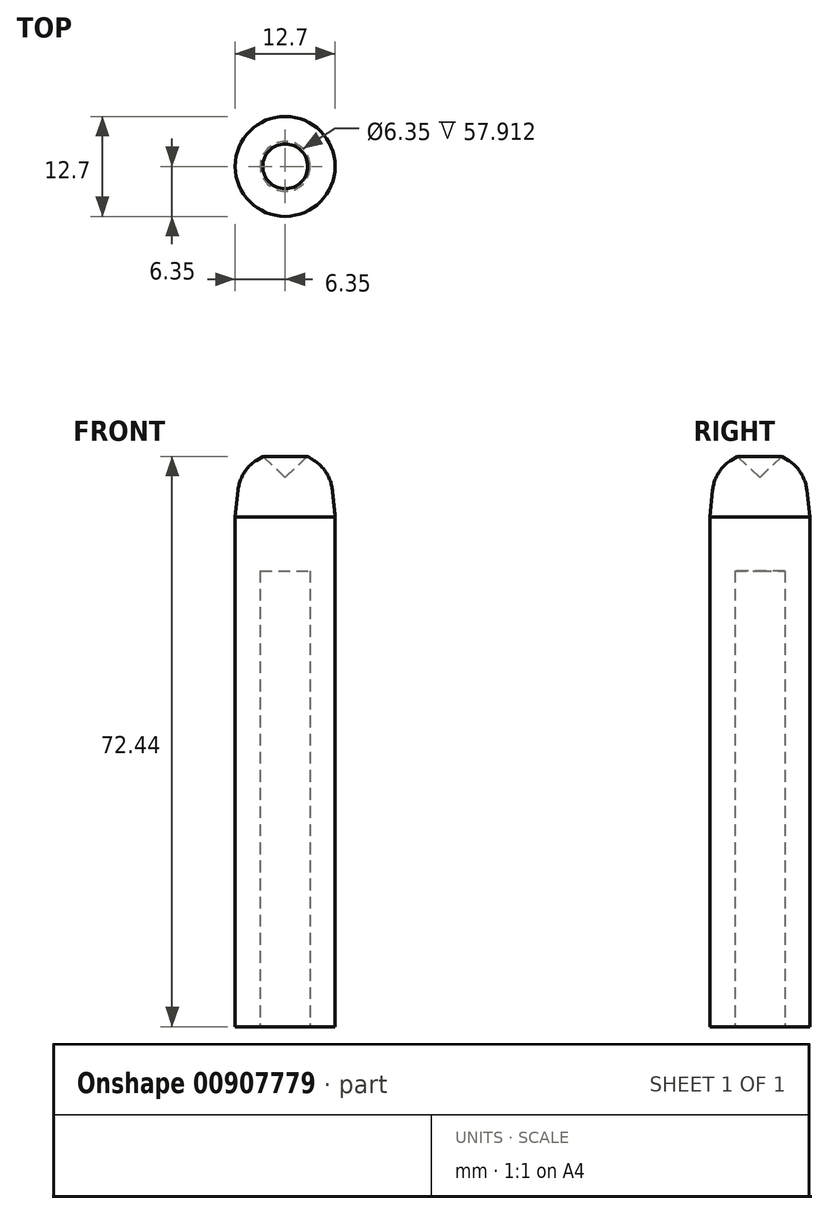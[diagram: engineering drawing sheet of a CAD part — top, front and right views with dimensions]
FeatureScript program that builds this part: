
annotation { "Feature Type Name" : "Feature", "Feature Type Description" : "" }
export const myFeature = defineFeature(function(context is Context, id is Id, definition is map)
    precondition{}
    {
        {
            var Q0;
            Q0=qCreatedBy(makeId("Top.planeOp"),FACE);
            var sketch = newSketch(context, id + "F0", { "sketchPlane" : qUnion([Q0])});
            skCircle(sketch, "E0", {"center": v(0, 0) * mm, "radius": 6.35 * mm});
            skSolve(sketch);
        }
        {
            var Q0;
            Q0=makeQuery(id+"F0.imprint","IMPRINT",FACE,{"disambiguationData":[TD([[makeQuery(id+"F0.imprint","IMPRINT",EDGE,{"derivedFrom":sQuery(id+"F0.wireOp",EDGE,"E0")}),1.0]])]});
            extrude(context, id + "F1", {"entities" : qUnion([Q0]), "depth" : 64.77 * mm, "offsetDistance" : 25.4 * mm});
        }
        {
            var Q0;
            Q0=qCreatedBy(makeId("Front.planeOp"),FACE);
            var sketch = newSketch(context, id + "F2", { "sketchPlane" : qUnion([Q0])});
            skLineSegment(sketch, "E1", {"start": v(0, 0) * mm, "end": v(0, 72.4) * mm, "construction": true});
            skSolve(sketch);
        }
        {
            var Q0;
            Q0=qCreatedBy(makeId("Front.planeOp"),FACE);
            var sketch = newSketch(context, id + "F3", { "sketchPlane" : qUnion([Q0])});
            skLineSegment(sketch, "E2", {"start": v(0, 69.8) * mm, "end": v(-2.85, 72.44) * mm});
            skLineSegment(sketch, "E3", {"start": v(-2.85, 72.44) * mm, "end": v(-5.73, 70.63) * mm});
            skLineSegment(sketch, "E4", {"start": v(-5.73, 70.63) * mm, "end": v(-6.35, 64.77) * mm});
            skLineSegment(sketch, "E5", {"start": v(-6.35, 64.77) * mm, "end": v(0, 64.77) * mm});
            skLineSegment(sketch, "E6", {"start": v(0, 64.77) * mm, "end": v(0, 69.8) * mm});
            skLineSegment(sketch, "E7.0", {"start": v(-6.35, 64.77) * mm, "end": v(6.35, 64.77) * mm});
            skSolve(sketch);
        }
        {
            var Q0;
            Q0=makeQuery(id+"F3.imprint","IMPRINT",FACE,{"disambiguationData":[TD([[makeQuery(id+"F3.imprint","IMPRINT",EDGE,{"derivedFrom":sQuery(id+"F3.wireOp",EDGE,"E2")}),1.0]])]});
            var Q1;
            Q1=sQuery(id+"F2.wireOp",EDGE,"E1");
            revolve(context, id + "F4", {"operationType" : NewBodyOperationType.ADD, "surfaceOperationType" : NewSurfaceOperationType.NEW, "entities" : qUnion([Q0]), "axis" : qUnion([Q1]), "revolveType" : RevolveType.FULL});
        }
        {
            var Q0;
            Q0=makeQuery(id+"F1.opExtrude","CAP_FACE",FACE,{"disambiguationData":[OSD([sQuery(id+"F0.wireOp",EDGE,"E0")])],"isStart":true});
            var sketch = newSketch(context, id + "F5", { "sketchPlane" : qUnion([Q0])});
            skCircle(sketch, "E8", {"center": v(0, 0) * mm, "radius": 3.17 * mm});
            skSolve(sketch);
        }
        {
            var Q0;
            Q0=makeQuery(id+"F5.imprint","IMPRINT",FACE,{"disambiguationData":[TD([[makeQuery(id+"F5.imprint","IMPRINT",EDGE,{"derivedFrom":sQuery(id+"F5.wireOp",EDGE,"E8")}),1.0]])]});
            extrude(context, id + "F6", {"entities" : qUnion([Q0]), "operationType" : NewBodyOperationType.REMOVE, "oppositeDirection" : true, "depth" : 57.9 * mm, "offsetDistance" : 25.4 * mm});
        }
        {
            var Q0;
            Q0=makeQuery(id+"F4.opRevolve","SWEPT_EDGE",EDGE,{"disambiguationData":[OSD([sQuery(id+"F3.wireOp",EDGE,"E3"),sQuery(id+"F3.wireOp",EDGE,"E4")])]});
            fillet(context, id + "F7", {"entities" : qUnion([Q0]), "radius" : 5.08 * mm, "tangentPropagation" : true, "allowEdgeOverflow" : false});
        }
    });
